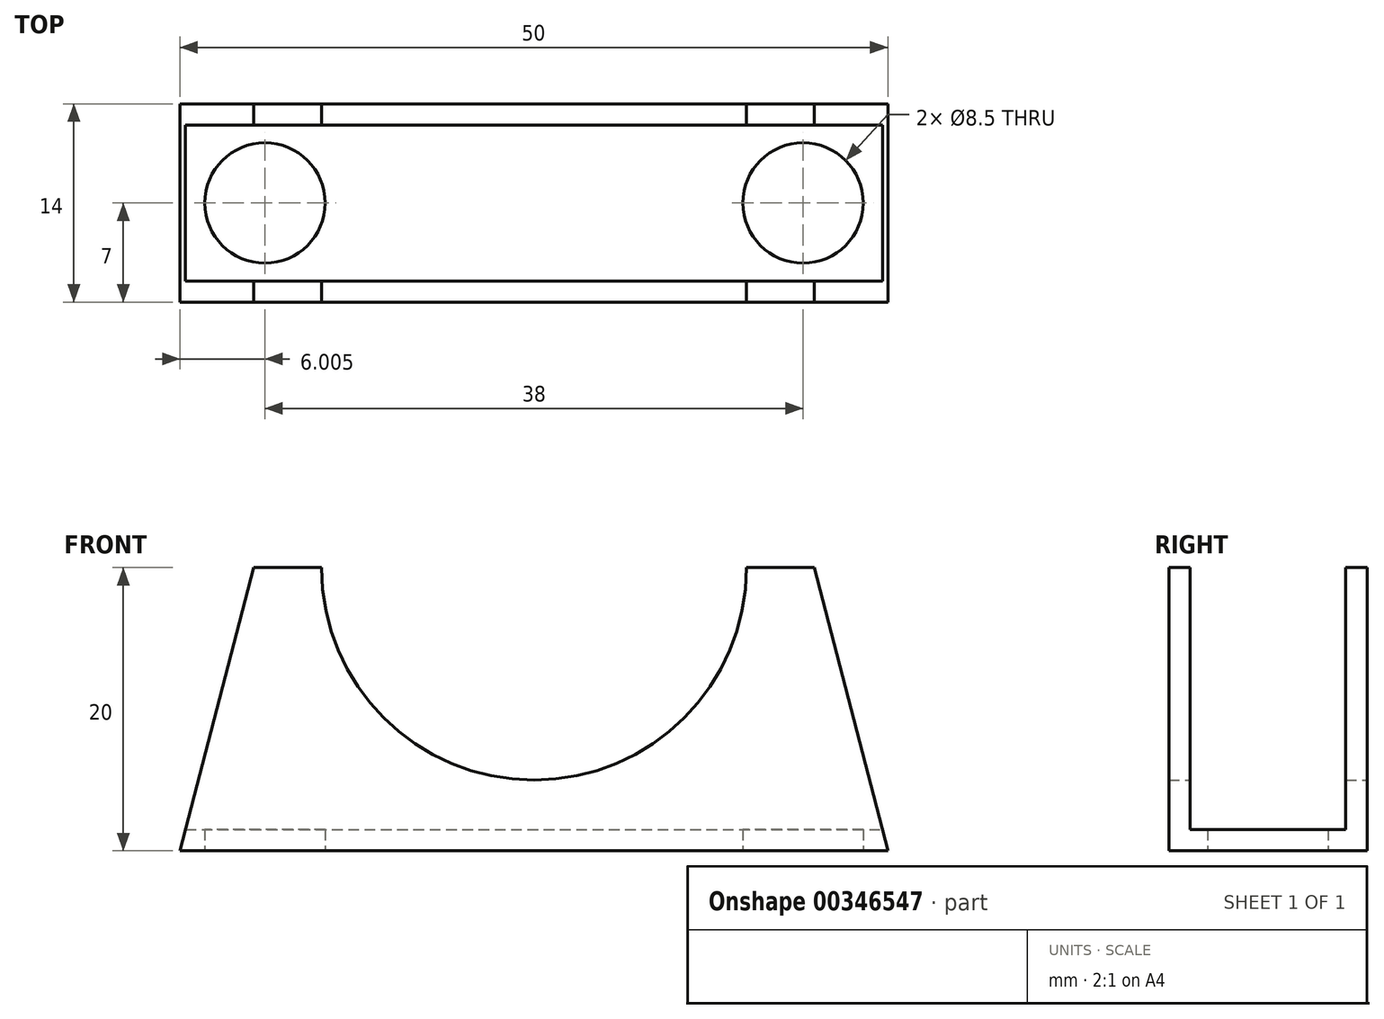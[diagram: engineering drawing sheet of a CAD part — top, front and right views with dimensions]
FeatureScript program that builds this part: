
annotation { "Feature Type Name" : "Feature", "Feature Type Description" : "" }
export const myFeature = defineFeature(function(context is Context, id is Id, definition is map)
    precondition{}
    {
        {
            var Q0;
            Q0=qCreatedBy(makeId("Front.planeOp"),FACE);
            var sketch = newSketch(context, id + "F0", { "sketchPlane" : qUnion([Q0])});
            skLineSegment(sketch, "E0", {"start": v(-59.09, 2.78) * mm, "end": v(-9.09, 2.78) * mm});
            skLineSegment(sketch, "E1", {"start": v(-9.09, 2.78) * mm, "end": v(-14.29, 22.78) * mm});
            skLineSegment(sketch, "E2", {"start": v(-14.29, 22.78) * mm, "end": v(-19.09, 22.78) * mm});
            skLineSegment(sketch, "E3", {"start": v(-59.09, 2.78) * mm, "end": v(-53.88, 22.78) * mm});
            skLineSegment(sketch, "E4", {"start": v(-53.88, 22.78) * mm, "end": v(-49.09, 22.78) * mm});
            skArc(sketch, "E5", {"start": v(-49.09, 22.78) * mm, "mid": v(-34.09, 7.78) * mm, "end": v(-19.09, 22.78) * mm});
            skLineSegment(sketch, "E6", {"start": v(-34.09, 22.78) * mm, "end": v(-34.09, -12.93) * mm, "construction": true});
            skSolve(sketch);
        }
        {
            var Q0;
            Q0 = qSketchRegion(id + "F0", true);
            extrude(context, id + "F1", {"entities" : qUnion([Q0]), "depth" : 14 * mm});
        }
        {
            var Q0;
            Q0=makeQuery(id+"F1.opExtrude","SWEPT_FACE",FACE,{"disambiguationData":[OSD([sQuery(id+"F0.wireOp",EDGE,"E3")])]});
            var Q1;
            Q1=makeQuery(id+"F1.opExtrude","SWEPT_FACE",FACE,{"disambiguationData":[OSD([sQuery(id+"F0.wireOp",EDGE,"E4")])]});
            var Q2;
            Q2=makeQuery(id+"F1.opExtrude","SWEPT_FACE",FACE,{"disambiguationData":[OSD([sQuery(id+"F0.wireOp",EDGE,"E5")])]});
            var Q3;
            Q3=makeQuery(id+"F1.opExtrude","SWEPT_FACE",FACE,{"disambiguationData":[OSD([sQuery(id+"F0.wireOp",EDGE,"E2")])]});
            var Q4;
            Q4=makeQuery(id+"F1.opExtrude","SWEPT_FACE",FACE,{"disambiguationData":[OSD([sQuery(id+"F0.wireOp",EDGE,"E1")])]});
            shell(context, id + "F2", {"entities" : qUnion([Q0, Q1, Q2, Q3, Q4]), "thickness" : 1.5 * mm});
        }
        {
            var Q0;
            Q0=makeQuery(id+"F1.opExtrude","SWEPT_FACE",FACE,{"disambiguationData":[OSD([sQuery(id+"F0.wireOp",EDGE,"E0")])]});
            var sketch = newSketch(context, id + "F3", { "sketchPlane" : qUnion([Q0])});
            skPoint(sketch, "E7", {"position": v(-53.09, 7) * mm});
            skPoint(sketch, "E8", {"position": v(-15.09, 7) * mm});
            skSolve(sketch);
        }
        {
            var Q0;
            Q0=sQuery(id+"F3.wireOp",VERTEX,"E7");
            var Q1;
            Q1=makeQuery(id+"F1.opExtrude","SWEPT_BODY",BODY,{"disambiguationData":[OSD([sQuery(id+"F0.wireOp",EDGE,"E0"),sQuery(id+"F0.wireOp",EDGE,"E1"),sQuery(id+"F0.wireOp",EDGE,"E2"),sQuery(id+"F0.wireOp",EDGE,"E3"),sQuery(id+"F0.wireOp",EDGE,"E4"),sQuery(id+"F0.wireOp",EDGE,"E5")])]});
            hole(context, id + "F4", {"style" : HoleStyle.SIMPLE, "endStyle" : HoleEndStyle.THROUGH, "holeDiameter" : 8.5 * mm, "isTappedThrough" : true, "tappedDepth" : 12 * mm, "tapClearance" : 3, "locations" : qUnion([Q0]), "scope" : qUnion([Q1])});
        }
        {
            var Q0;
            Q0=sQuery(id+"F3.wireOp",VERTEX,"E8");
            var Q1;
            Q1=makeQuery(id+"F1.opExtrude","SWEPT_BODY",BODY,{"disambiguationData":[OSD([sQuery(id+"F0.wireOp",EDGE,"E0"),sQuery(id+"F0.wireOp",EDGE,"E1"),sQuery(id+"F0.wireOp",EDGE,"E2"),sQuery(id+"F0.wireOp",EDGE,"E3"),sQuery(id+"F0.wireOp",EDGE,"E4"),sQuery(id+"F0.wireOp",EDGE,"E5")])]});
            hole(context, id + "F5", {"style" : HoleStyle.SIMPLE, "endStyle" : HoleEndStyle.THROUGH, "holeDiameter" : 8.5 * mm, "isTappedThrough" : true, "tappedDepth" : 12 * mm, "tapClearance" : 3, "locations" : qUnion([Q0]), "scope" : qUnion([Q1])});
        }
    });
